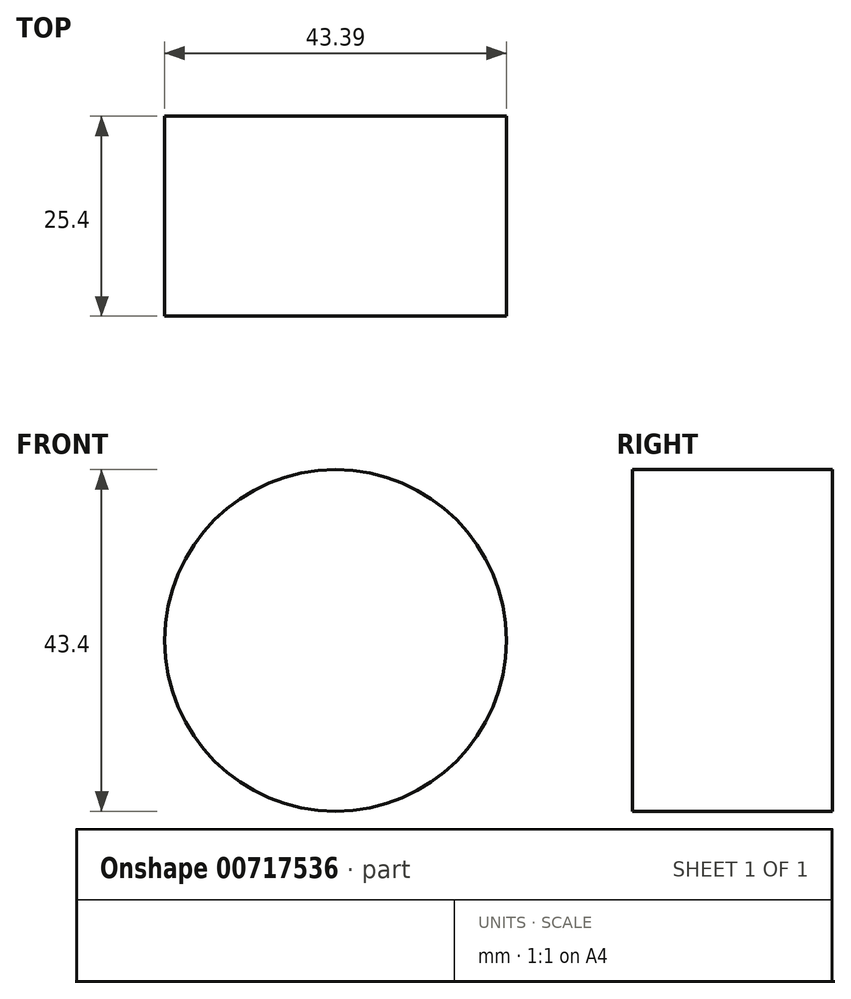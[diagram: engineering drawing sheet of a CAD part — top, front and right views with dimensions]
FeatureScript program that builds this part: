
annotation { "Feature Type Name" : "Feature", "Feature Type Description" : "" }
export const myFeature = defineFeature(function(context is Context, id is Id, definition is map)
    precondition{}
    {
        {
            var Q0;
            Q0=qCreatedBy(makeId("Front.planeOp"),FACE);
            var sketch = newSketch(context, id + "F0", { "sketchPlane" : qUnion([Q0])});
            skCircle(sketch, "E0", {"center": v(44.97, 51.55) * mm, "radius": 21.7 * mm});
            skSolve(sketch);
        }
        {
            var Q0;
            Q0=makeQuery(id+"F0.imprint","IMPRINT",FACE,{"disambiguationData":[TD([[makeQuery(id+"F0.imprint","IMPRINT",EDGE,{"derivedFrom":sQuery(id+"F0.wireOp",EDGE,"E0")}),1.0]])]});
            var Q1;
            Q1=sQuery(id+"F0.wireOp",EDGE,"E0");
            extrude(context, id + "F1", {"entities" : qUnion([Q0]), "surfaceEntities" : qUnion([Q1]), "depth" : 25.4 * mm, "offsetDistance" : 25.4 * mm});
        }
    });
